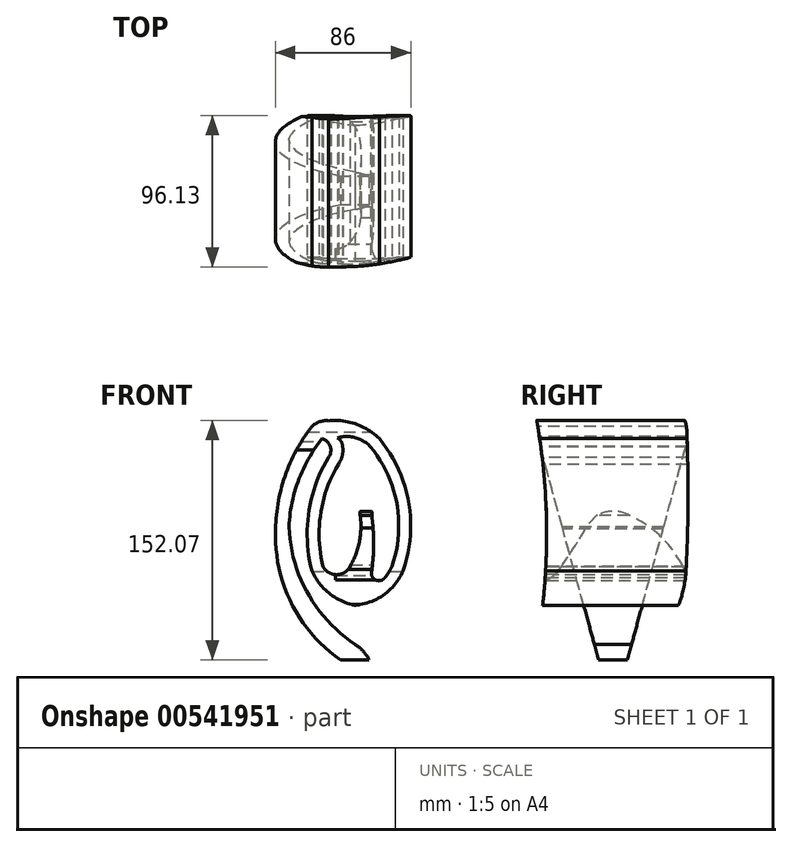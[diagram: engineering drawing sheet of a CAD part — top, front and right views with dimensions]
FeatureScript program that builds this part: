
annotation { "Feature Type Name" : "Feature", "Feature Type Description" : "" }
export const myFeature = defineFeature(function(context is Context, id is Id, definition is map)
    precondition{}
    {
        {
            var Q0;
            Q0=qCreatedBy(makeId("Right.planeOp"),FACE);
            var sketch = newSketch(context, id + "F0", { "sketchPlane" : qUnion([Q0])});
            skLineSegment(sketch, "E0", {"start": v(0, 0) * mm, "end": v(0, 152.4) * mm});
            skLineSegment(sketch, "E1", {"start": v(0, 152.4) * mm, "end": v(-50.8, 152.4) * mm});
            skLineSegment(sketch, "E2", {"start": v(-50.8, 152.4) * mm, "end": v(-9.14, 0) * mm});
            skLineSegment(sketch, "E3", {"start": v(-9.14, 0) * mm, "end": v(0, 0) * mm});
            skLineSegment(sketch, "E4.MirrorCS", {"start": v(0, 152.4) * mm, "end": v(50.8, 152.4) * mm});
            skLineSegment(sketch, "E5.MirrorCS", {"start": v(50.8, 152.4) * mm, "end": v(9.14, 0) * mm});
            skLineSegment(sketch, "E6.MirrorCS", {"start": v(9.14, 0) * mm, "end": v(0, 0) * mm});
            skSolve(sketch);
        }
        {
            var Q0;
            Q0 = qSketchRegion(id + "F0", true);
            extrude(context, id + "F1", {"entities" : qUnion([Q0]), "endBound" : BoundingType.SYMMETRIC, "depth" : 101.6 * mm, "offsetDistance" : 25.4 * mm});
        }
        {
            var Q0;
            Q0=qCreatedBy(makeId("Front.planeOp"),FACE);
            var sketch = newSketch(context, id + "F2", { "sketchPlane" : qUnion([Q0])});
            skArc(sketch, "E7", {"start": v(-50.34, 83.03) * mm, "mid": v(-40.41, 36.22) * mm, "end": v(-9.14, 0) * mm});
            skArc(sketch, "E8", {"start": v(-27.3, 148.16) * mm, "mid": v(-44.07, 117.45) * mm, "end": v(-50.34, 83.03) * mm});
            skArc(sketch, "E9", {"start": v(-16.78, 151.86) * mm, "mid": v(-22.47, 151.23) * mm, "end": v(-27.3, 148.16) * mm});
            skArc(sketch, "E10", {"start": v(15.64, 140.48) * mm, "mid": v(0.7, 149.8) * mm, "end": v(-16.78, 151.86) * mm});
            skArc(sketch, "E11", {"start": v(30.71, 56.59) * mm, "mid": v(34.21, 100.52) * mm, "end": v(15.64, 140.48) * mm});
            skArc(sketch, "E12", {"start": v(0, 34.69) * mm, "mid": v(18.41, 41.35) * mm, "end": v(30.71, 56.59) * mm});
            skArc(sketch, "E13", {"start": v(-27.3, 56.59) * mm, "mid": v(-16.29, 42.35) * mm, "end": v(0, 34.69) * mm});
            skArc(sketch, "E14", {"start": v(-16.78, 128.54) * mm, "mid": v(-29.26, 93.62) * mm, "end": v(-27.3, 56.59) * mm});
            skArc(sketch, "E15", {"start": v(-16.78, 128.54) * mm, "mid": v(-15.55, 135.58) * mm, "end": v(-20.76, 140.48) * mm});
            skArc(sketch, "E16", {"start": v(-20.76, 140.48) * mm, "mid": v(-35.73, 114.14) * mm, "end": v(-41.8, 84.46) * mm});
            skArc(sketch, "E17", {"start": v(-41.8, 84.46) * mm, "mid": v(-29.85, 42.18) * mm, "end": v(0, 9.94) * mm});
            skArc(sketch, "E18", {"start": v(9.14, 0) * mm, "mid": v(5.23, 5.58) * mm, "end": v(0, 9.94) * mm});
            skLineSegment(sketch, "E19", {"start": v(-9.14, 0) * mm, "end": v(-55.18, 0) * mm});
            skLineSegment(sketch, "E20", {"start": v(-55.18, 0) * mm, "end": v(-55.18, 155.27) * mm});
            skLineSegment(sketch, "E21", {"start": v(-55.18, 155.27) * mm, "end": v(56.59, 155.27) * mm});
            skLineSegment(sketch, "E22", {"start": v(56.59, 155.27) * mm, "end": v(56.59, -2) * mm});
            skLineSegment(sketch, "E23", {"start": v(56.59, -2) * mm, "end": v(9.14, 0) * mm});
            skSolve(sketch);
        }
        {
            var Q0;
            Q0 = qSketchRegion(id + "F2", true);
            extrude(context, id + "F3", {"entities" : qUnion([Q0]), "operationType" : NewBodyOperationType.REMOVE, "endBound" : BoundingType.SYMMETRIC, "oppositeDirection" : true, "depth" : 203.2 * mm, "offsetDistance" : 25.4 * mm});
        }
        {
            var Q0;
            Q0=qCreatedBy(makeId("Front.planeOp"),FACE);
            var sketch = newSketch(context, id + "F4", { "sketchPlane" : qUnion([Q0])});
            skArc(sketch, "E24.0", {"start": v(-16.78, 151.86) * mm, "mid": v(0.7, 149.8) * mm, "end": v(15.64, 140.48) * mm});
            skArc(sketch, "E25.0", {"start": v(15.64, 140.48) * mm, "mid": v(34.21, 100.52) * mm, "end": v(30.71, 56.59) * mm});
            skArc(sketch, "E26.0", {"start": v(30.71, 56.59) * mm, "mid": v(18.41, 41.35) * mm, "end": v(0, 34.69) * mm});
            skArc(sketch, "E27.0", {"start": v(0, 34.69) * mm, "mid": v(-16.29, 42.35) * mm, "end": v(-27.3, 56.59) * mm});
            skArc(sketch, "E28.0", {"start": v(-27.3, 56.59) * mm, "mid": v(-29.26, 93.62) * mm, "end": v(-16.78, 128.54) * mm});
            skArc(sketch, "E29.0", {"start": v(-20.76, 140.48) * mm, "mid": v(-15.55, 135.58) * mm, "end": v(-16.78, 128.54) * mm});
            skLineSegment(sketch, "E30", {"start": v(-16.78, 151.86) * mm, "end": v(-20.76, 140.48) * mm});
            skSolve(sketch);
        }
        {
            var Q0;
            Q0 = qSketchRegion(id + "F4", true);
            extrude(context, id + "F5", {"entities" : qUnion([Q0]), "operationType" : NewBodyOperationType.ADD, "endBound" : BoundingType.SYMMETRIC, "depth" : 96.52 * mm, "offsetDistance" : 25.4 * mm});
        }
        {
            var Q0;
            Q0=makeQuery(id+"F5.opExtrude","CAP_FACE",FACE,{"disambiguationData":[OSD([sQuery(id+"F4.wireOp",EDGE,"E24.0"),sQuery(id+"F4.wireOp",EDGE,"E25.0"),sQuery(id+"F4.wireOp",EDGE,"E26.0"),sQuery(id+"F4.wireOp",EDGE,"E27.0"),sQuery(id+"F4.wireOp",EDGE,"E28.0"),sQuery(id+"F4.wireOp",EDGE,"E29.0"),sQuery(id+"F4.wireOp",EDGE,"E30")])],"isStart":false});
            var sketch = newSketch(context, id + "F6", { "sketchPlane" : qUnion([Q0])});
            skArc(sketch, "E31.0", {"start": v(10.03, 135.31) * mm, "mid": v(9.94, 135.4) * mm, "end": v(9.85, 135.49) * mm});
            skArc(sketch, "E31.1", {"start": v(23.61, 59.37) * mm, "mid": v(26.72, 99.11) * mm, "end": v(10.03, 135.31) * mm});
            skArc(sketch, "E31.2", {"start": v(-7.72, 135.49) * mm, "mid": v(-7.97, 129.61) * mm, "end": v(-10.45, 124.28) * mm});
            skArc(sketch, "E31.3", {"start": v(-10.45, 124.28) * mm, "mid": v(-21.7, 92.66) * mm, "end": v(-20.09, 59.13) * mm});
            skArc(sketch, "E31.6", {"start": v(18.57, 51.63) * mm, "mid": v(21.4, 55.3) * mm, "end": v(23.61, 59.37) * mm});
            skArc(sketch, "E32", {"start": v(-3.62, 58.38) * mm, "mid": v(2.84, 74.52) * mm, "end": v(3.4, 91.88) * mm});
            skArc(sketch, "E33", {"start": v(10.8, 91.88) * mm, "mid": v(7.1, 96.7) * mm, "end": v(3.4, 91.88) * mm});
            skArc(sketch, "E34", {"start": v(10.8, 56.59) * mm, "mid": v(11.98, 74.24) * mm, "end": v(10.8, 91.88) * mm});
            skArc(sketch, "E35", {"start": v(-20.09, 59.13) * mm, "mid": v(-11.62, 54.11) * mm, "end": v(-3.16, 59.13) * mm});
            skPoint(sketch, "E36.orphan", {"position": v(-11.7, 48.43) * mm});
            skArc(sketch, "E37", {"start": v(10.8, 56.59) * mm, "mid": v(13.04, 50.86) * mm, "end": v(19.06, 52.17) * mm});
            skArc(sketch, "E38", {"start": v(-7.72, 135.49) * mm, "mid": v(-8.65, 138.7) * mm, "end": v(-11.07, 141.01) * mm});
            skArc(sketch, "E39", {"start": v(10.03, 135.31) * mm, "mid": v(0.28, 141.15) * mm, "end": v(-11.07, 141.01) * mm});
            skSolve(sketch);
        }
        {
            var Q0;
            Q0 = qSketchRegion(id + "F6", true);
            extrude(context, id + "F7", {"entities" : qUnion([Q0]), "operationType" : NewBodyOperationType.REMOVE, "endBound" : BoundingType.THROUGH_ALL, "oppositeDirection" : true, "depth" : 25.4 * mm, "offsetDistance" : 25.4 * mm});
        }
        {
            var Q0;
            Q0=qCreatedBy(makeId("Right.planeOp"),FACE);
            var sketch = newSketch(context, id + "F8", { "sketchPlane" : qUnion([Q0])});
            skArc(sketch, "E40", {"start": v(-44.58, 35.1) * mm, "mid": v(-42.4, 94.88) * mm, "end": v(-48.84, 154.36) * mm});
            skArc(sketch, "E41", {"start": v(-52.25, 30.83) * mm, "mid": v(-47.48, 31.28) * mm, "end": v(-44.58, 35.1) * mm});
            skArc(sketch, "E42", {"start": v(-63.33, 154.07) * mm, "mid": v(-67.76, 91.56) * mm, "end": v(-52.25, 30.83) * mm});
            skArc(sketch, "E43", {"start": v(-48.84, 154.36) * mm, "mid": v(-56.2, 160.5) * mm, "end": v(-63.33, 154.07) * mm});
            skSolve(sketch);
        }
        {
            var Q0;
            Q0 = qSketchRegion(id + "F8", true);
            extrude(context, id + "F9", {"entities" : qUnion([Q0]), "operationType" : NewBodyOperationType.REMOVE, "endBound" : BoundingType.SYMMETRIC, "oppositeDirection" : true, "depth" : 152.4 * mm, "offsetDistance" : 25.4 * mm});
        }
        {
            var Q0;
            Q0=qCreatedBy(makeId("Right.planeOp"),FACE);
            var sketch = newSketch(context, id + "F10", { "sketchPlane" : qUnion([Q0])});
            skArc(sketch, "E44", {"start": v(46.86, 144.7) * mm, "mid": v(46.36, 149.68) * mm, "end": v(44.58, 154.36) * mm});
            skArc(sketch, "E45", {"start": v(46.36, 56.1) * mm, "mid": v(47.68, 100.4) * mm, "end": v(46.86, 144.7) * mm});
            skPoint(sketch, "E45.startSnap0", {"position": v(46.36, 149.68) * mm});
            skArc(sketch, "E46", {"start": v(40.32, 31.4) * mm, "mid": v(44.42, 43.49) * mm, "end": v(46.36, 56.1) * mm});
            skArc(sketch, "E47", {"start": v(40.32, 31.4) * mm, "mid": v(39.33, 23.01) * mm, "end": v(46.86, 19.19) * mm});
            skArc(sketch, "E48", {"start": v(46.86, 19.19) * mm, "mid": v(63.91, 71.12) * mm, "end": v(60.49, 125.68) * mm});
            skArc(sketch, "E49", {"start": v(60.49, 125.68) * mm, "mid": v(59.89, 140.76) * mm, "end": v(53.95, 154.64) * mm});
            skArc(sketch, "E50", {"start": v(53.95, 154.64) * mm, "mid": v(49.2, 156.6) * mm, "end": v(44.58, 154.36) * mm});
            skSolve(sketch);
        }
        {
            var Q0;
            Q0 = qSketchRegion(id + "F10", true);
            extrude(context, id + "F11", {"entities" : qUnion([Q0]), "operationType" : NewBodyOperationType.REMOVE, "endBound" : BoundingType.SYMMETRIC, "oppositeDirection" : true, "depth" : 152.4 * mm, "offsetDistance" : 25.4 * mm});
        }
        {
            var Q0;
            Q0=qCreatedBy(makeId("Right.planeOp"),FACE);
            var sketch = newSketch(context, id + "F12", { "sketchPlane" : qUnion([Q0])});
            skLineSegment(sketch, "E51", {"start": v(0, 51.12) * mm, "end": v(0, 96.94) * mm, "construction": true});
            skLineSegment(sketch, "E52", {"start": v(51.38, 51.12) * mm, "end": v(51.38, 108.84) * mm});
            skLineSegment(sketch, "E53", {"start": v(51.38, 108.84) * mm, "end": v(-52.36, 108.84) * mm});
            skLineSegment(sketch, "E54", {"start": v(-52.36, 108.84) * mm, "end": v(-52.36, 51.12) * mm});
            skArc(sketch, "E55", {"start": v(46.25, 51.12) * mm, "mid": v(45.72, 55.83) * mm, "end": v(43.99, 60.24) * mm});
            skArc(sketch, "E56", {"start": v(43.99, 60.24) * mm, "mid": v(29.78, 78.83) * mm, "end": v(10.36, 91.89) * mm});
            skArc(sketch, "E57", {"start": v(10.36, 91.89) * mm, "mid": v(0.2, 94.44) * mm, "end": v(-9.98, 91.89) * mm});
            skArc(sketch, "E58", {"start": v(-9.98, 91.89) * mm, "mid": v(-13.92, 88.14) * mm, "end": v(-17.05, 83.7) * mm});
            skArc(sketch, "E59", {"start": v(-34, 57.41) * mm, "mid": v(-25.38, 70.46) * mm, "end": v(-17.05, 83.7) * mm});
            skArc(sketch, "E60", {"start": v(-52.36, 51.12) * mm, "mid": v(-42.1, 51.09) * mm, "end": v(-34, 57.41) * mm});
            skLineSegment(sketch, "E61", {"start": v(46.25, 51.12) * mm, "end": v(51.38, 51.12) * mm});
            skSolve(sketch);
        }
        {
            var Q0;
            Q0 = qSketchRegion(id + "F12", true);
            extrude(context, id + "F13", {"entities" : qUnion([Q0]), "operationType" : NewBodyOperationType.REMOVE, "oppositeDirection" : true, "depth" : 12.2 * mm, "offsetDistance" : 25.4 * mm, "hasSecondDirection" : true, "secondDirectionOppositeDirection" : false, "secondDirectionDepth" : 17.78 * mm});
        }
    });
